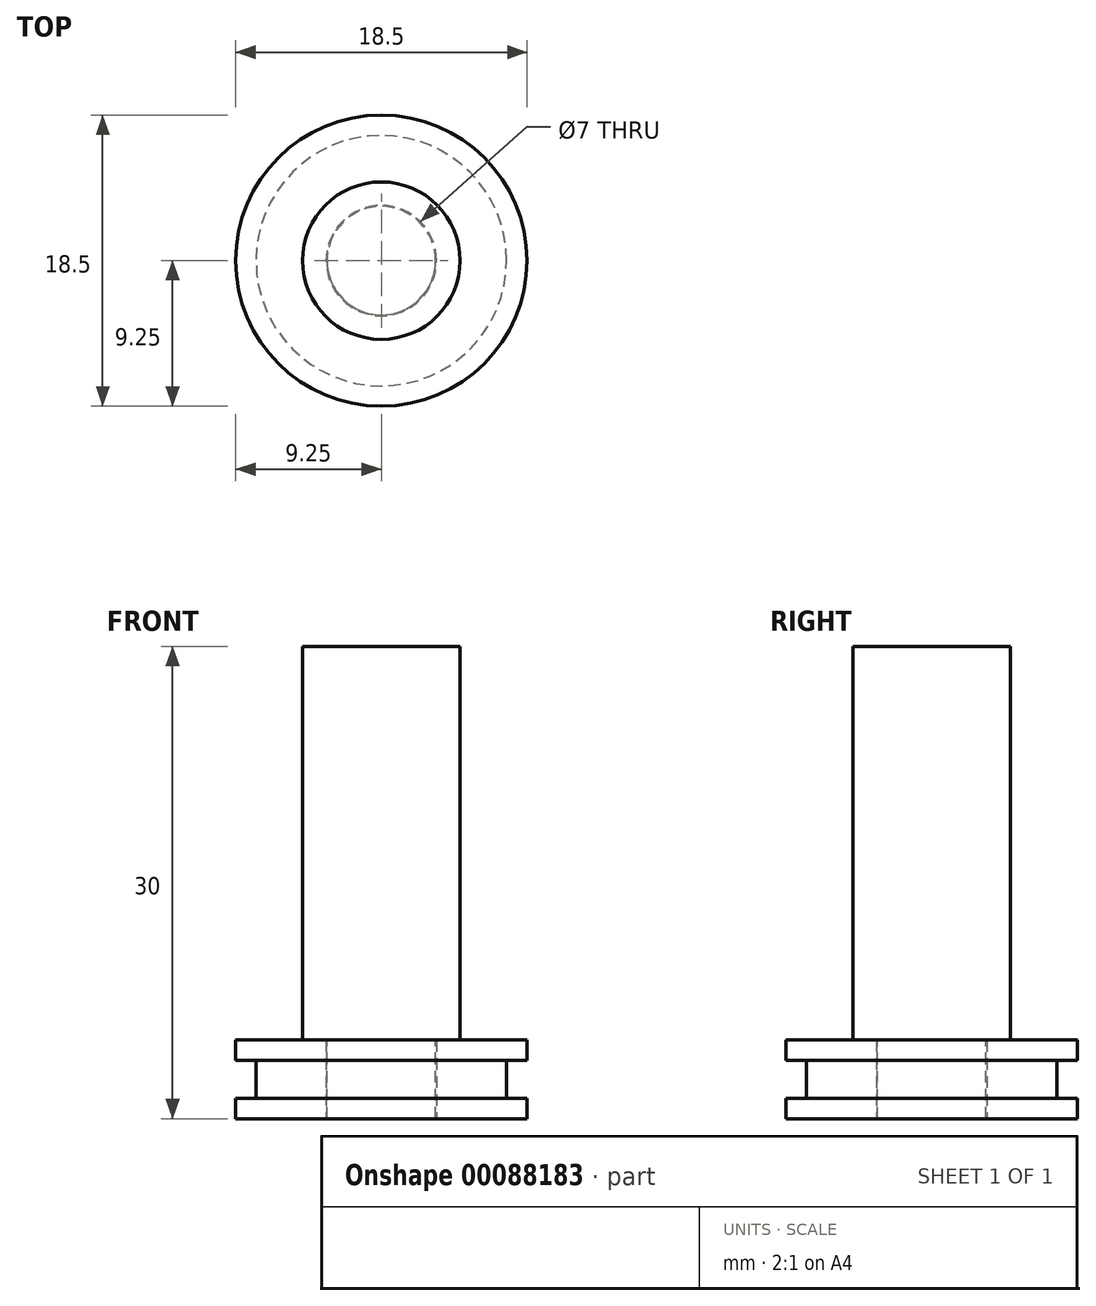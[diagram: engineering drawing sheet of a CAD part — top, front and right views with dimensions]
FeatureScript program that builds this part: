
annotation { "Feature Type Name" : "Feature", "Feature Type Description" : "" }
export const myFeature = defineFeature(function(context is Context, id is Id, definition is map)
    precondition{}
    {
        {
            var Q0;
            Q0=qCreatedBy(makeId("Top.planeOp"),FACE);
            var sketch = newSketch(context, id + "F0", { "sketchPlane" : qUnion([Q0])});
            skCircle(sketch, "E0", {"center": v(0, 0) * mm, "radius": 9.25 * mm});
            skCircle(sketch, "E1", {"center": v(0, 0) * mm, "radius": 3.5 * mm});
            skSolve(sketch);
        }
        {
            var Q0;
            Q0=makeQuery(id+"F0.imprint","IMPRINT",FACE,{"disambiguationData":[TD([[makeQuery(id+"F0.imprint","IMPRINT",EDGE,{"derivedFrom":sQuery(id+"F0.wireOp",EDGE,"E0")}),1.0]])]});
            extrude(context, id + "F1", {"entities" : qUnion([Q0]), "endBound" : BoundingType.SYMMETRIC, "depth" : 5 * mm});
        }
        {
            var Q0;
            Q0=qCreatedBy(makeId("Top.planeOp"),FACE);
            var sketch = newSketch(context, id + "F2", { "sketchPlane" : qUnion([Q0])});
            skCircle(sketch, "E2", {"center": v(0, 0) * mm, "radius": 7.95 * mm});
            skCircle(sketch, "E3", {"center": v(0, 0) * mm, "radius": 22.5 * mm});
            skSolve(sketch);
        }
        {
            var Q0;
            Q0 = qSketchRegion(id + "F2", true);
            extrude(context, id + "F3", {"entities" : qUnion([Q0]), "operationType" : NewBodyOperationType.REMOVE, "endBound" : BoundingType.SYMMETRIC, "depth" : 2.41 * mm});
        }
        {
            var Q0;
            Q0=makeQuery(id+"F1.opExtrude","CAP_FACE",FACE,{"disambiguationData":[OSD([sQuery(id+"F0.wireOp",EDGE,"E0")])],"isStart":false});
            var sketch = newSketch(context, id + "F4", { "sketchPlane" : qUnion([Q0])});
            skCircle(sketch, "E4", {"center": v(0, 0) * mm, "radius": 5 * mm});
            skSolve(sketch);
        }
        {
            var Q0;
            Q0 = qSketchRegion(id + "F4", true);
            extrude(context, id + "F5", {"entities" : qUnion([Q0]), "depth" : 25 * mm});
        }
        {
            var Q0;
            Q0=makeQuery(id+"F5.opExtrude","CAP_FACE",FACE,{"disambiguationData":[OSD([sQuery(id+"F4.wireOp",EDGE,"E4")])],"isStart":true});
            var sketch = newSketch(context, id + "F6", { "sketchPlane" : qUnion([Q0])});
            skCircle(sketch, "E5", {"center": v(0, 0) * mm, "radius": 3.45 * mm});
            skSolve(sketch);
        }
        {
            var Q0;
            Q0 = qSketchRegion(id + "F6", true);
            var Q1;
            Q1=makeQuery(id+"F1.opExtrude","CAP_FACE",FACE,{"disambiguationData":[OSD([sQuery(id+"F0.wireOp",EDGE,"E0"),sQuery(id+"F0.wireOp",EDGE,"E1")])],"isStart":true});
            extrude(context, id + "F7", {"entities" : qUnion([Q0]), "operationType" : NewBodyOperationType.ADD, "endBound" : BoundingType.UP_TO_SURFACE, "endBoundEntityFace" : qUnion([Q1]), "depth" : 25 * mm});
        }
    });
